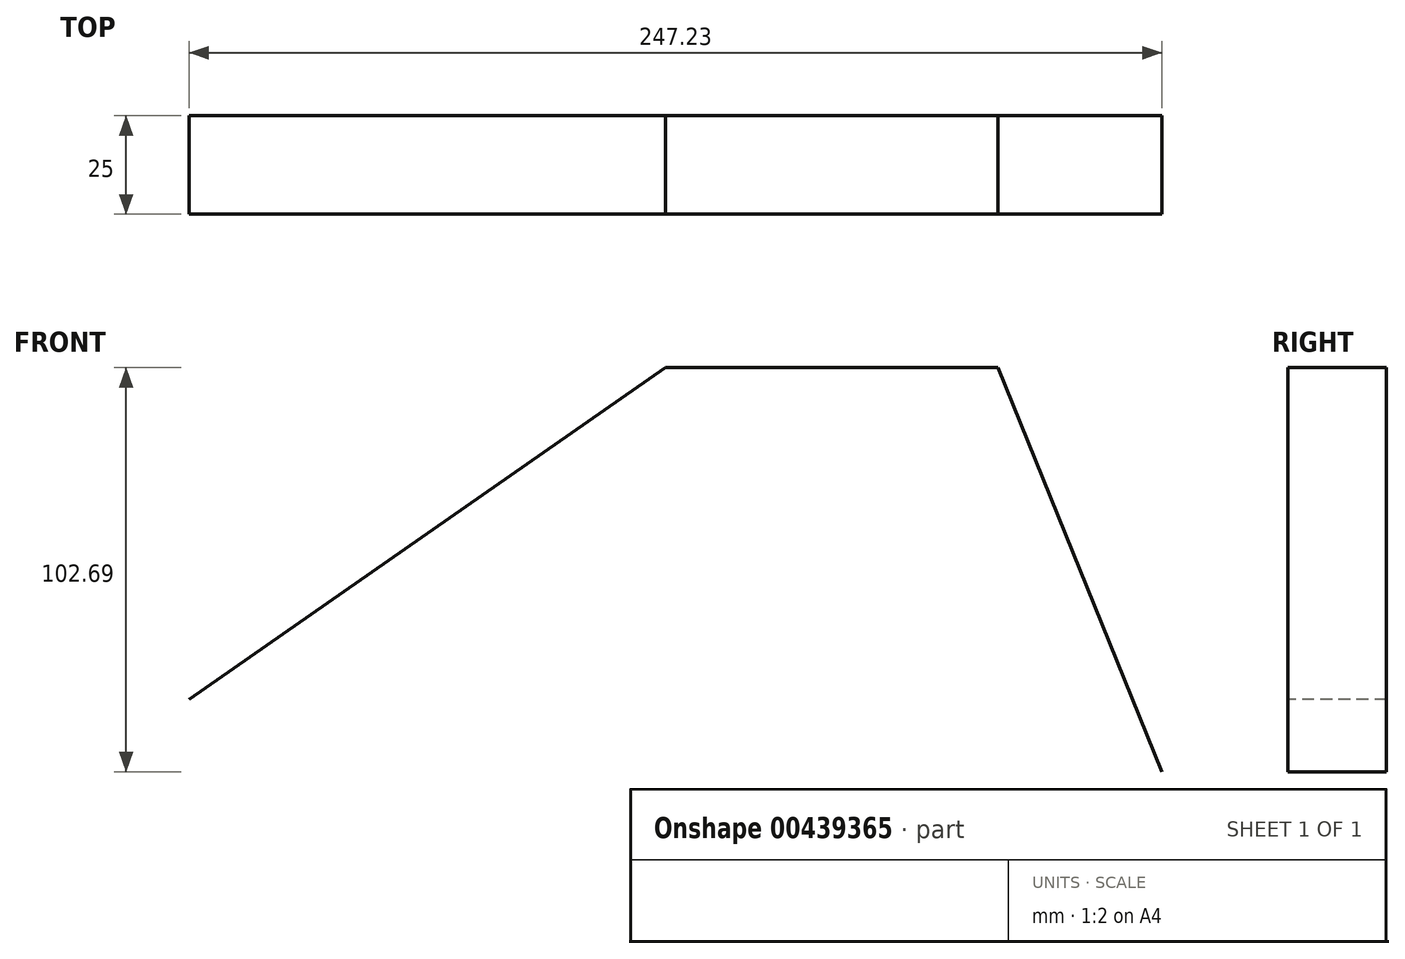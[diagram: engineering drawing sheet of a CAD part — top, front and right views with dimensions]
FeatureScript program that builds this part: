
annotation { "Feature Type Name" : "Feature", "Feature Type Description" : "" }
export const myFeature = defineFeature(function(context is Context, id is Id, definition is map)
    precondition{}
    {
        {
            var Q0;
            Q0=qCreatedBy(makeId("Front.planeOp"),FACE);
            var sketch = newSketch(context, id + "F0", { "sketchPlane" : qUnion([Q0])});
            skLineSegment(sketch, "E0", {"start": v(-111.73, 15.29) * mm, "end": v(9.38, 99.55) * mm});
            skLineSegment(sketch, "E1", {"start": v(9.38, 99.55) * mm, "end": v(93.73, 99.55) * mm});
            skLineSegment(sketch, "E2", {"start": v(93.73, 99.55) * mm, "end": v(135.5, -3.14) * mm});
            skSolve(sketch);
        }
        {
            var Q0;
            Q0 = qSketchRegion(id + "F0", true);
            var Q1;
            Q1=sQuery(id+"F0.wireOp",EDGE,"E0");
            var Q2;
            Q2=sQuery(id+"F0.wireOp",EDGE,"E1");
            var Q3;
            Q3=sQuery(id+"F0.wireOp",EDGE,"E2");
            extrude(context, id + "F1", {"entities" : qUnion([Q0]), "bodyType" : ToolBodyType.SURFACE, "surfaceEntities" : qUnion([Q1, Q2, Q3]), "depth" : 25 * mm, "symmetric" : true});
        }
    });
